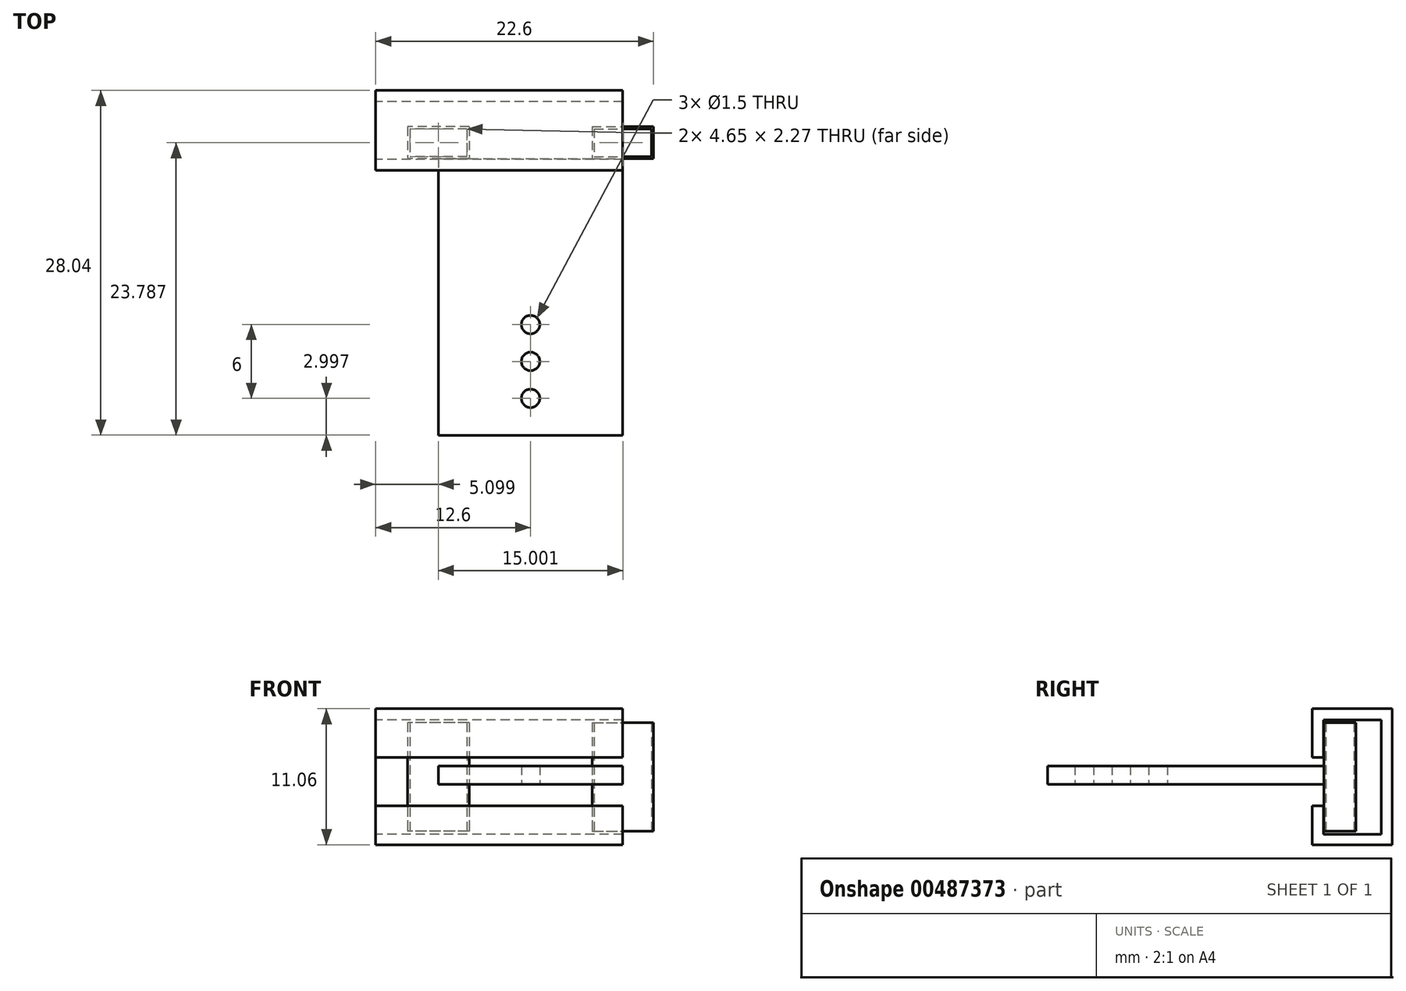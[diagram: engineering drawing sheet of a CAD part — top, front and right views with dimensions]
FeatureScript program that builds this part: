
annotation { "Feature Type Name" : "Feature", "Feature Type Description" : "" }
export const myFeature = defineFeature(function(context is Context, id is Id, definition is map)
    precondition{}
    {
        {
            var Q0;
            Q0=qCreatedBy(makeId("Top.planeOp"),FACE);
            var sketch = newSketch(context, id + "F0", { "sketchPlane" : qUnion([Q0])});
            skLineSegment(sketch, "E0.bottom", {"start": v(-7.5, 5.49) * mm, "end": v(7.5, 5.49) * mm});
            skLineSegment(sketch, "E0.top", {"start": v(-7.5, -17.01) * mm, "end": v(7.5, -17.01) * mm});
            skLineSegment(sketch, "E0.left", {"start": v(-7.5, 5.49) * mm, "end": v(-7.5, -17.01) * mm});
            skLineSegment(sketch, "E0.right", {"start": v(7.5, 5.49) * mm, "end": v(7.5, -17.01) * mm});
            skSolve(sketch);
        }
        {
            var Q0;
            Q0 = qSketchRegion(id + "F0", true);
            extrude(context, id + "F1", {"entities" : qUnion([Q0]), "depth" : 1.5 * mm, "offsetDistance" : 25 * mm});
        }
        {
            var Q0;
            Q0=qCreatedBy(makeId("Top.planeOp"),FACE);
            var sketch = newSketch(context, id + "F2", { "sketchPlane" : qUnion([Q0])});
            skLineSegment(sketch, "E1.bottom", {"start": v(5, 8.07) * mm, "end": v(10, 8.07) * mm});
            skLineSegment(sketch, "E1.top", {"start": v(5, 5.49) * mm, "end": v(10, 5.49) * mm});
            skLineSegment(sketch, "E1.left", {"start": v(5, 8.07) * mm, "end": v(5, 5.49) * mm});
            skLineSegment(sketch, "E1.right", {"start": v(10, 8.07) * mm, "end": v(10, 5.49) * mm});
            skLineSegment(sketch, "E2.MirrorCS", {"start": v(-5, 8.07) * mm, "end": v(-5, 5.49) * mm});
            skLineSegment(sketch, "E3.MirrorCS", {"start": v(-5, 8.07) * mm, "end": v(-10, 8.07) * mm});
            skLineSegment(sketch, "E4.MirrorCS", {"start": v(-10, 8.07) * mm, "end": v(-10, 5.49) * mm});
            skLineSegment(sketch, "E5.MirrorCS", {"start": v(-5, 5.49) * mm, "end": v(-10, 5.49) * mm});
            skLineSegment(sketch, "E6.bottom", {"start": v(5.18, 7.91) * mm, "end": v(9.83, 7.91) * mm});
            skLineSegment(sketch, "E6.top", {"start": v(5.18, 5.64) * mm, "end": v(9.83, 5.64) * mm});
            skLineSegment(sketch, "E6.left", {"start": v(5.18, 7.91) * mm, "end": v(5.18, 5.64) * mm});
            skLineSegment(sketch, "E6.right", {"start": v(9.83, 7.91) * mm, "end": v(9.83, 5.64) * mm});
            skLineSegment(sketch, "E7.MirrorCS", {"start": v(-5.18, 7.91) * mm, "end": v(-9.83, 7.91) * mm});
            skLineSegment(sketch, "E8.MirrorCS", {"start": v(-5.18, 7.91) * mm, "end": v(-5.18, 5.64) * mm});
            skLineSegment(sketch, "E9.MirrorCS", {"start": v(-5.18, 5.64) * mm, "end": v(-9.83, 5.64) * mm});
            skLineSegment(sketch, "E10.MirrorCS", {"start": v(-9.83, 7.91) * mm, "end": v(-9.83, 5.64) * mm});
            skSolve(sketch);
        }
        {
            var Q0;
            Q0 = qSketchRegion(id + "F2", true);
            extrude(context, id + "F3", {"entities" : qUnion([Q0]), "operationType" : NewBodyOperationType.ADD, "depth" : 5 * mm, "offsetDistance" : 25 * mm, "hasSecondDirection" : true, "secondDirectionOppositeDirection" : true, "secondDirectionDepth" : 3.8 * mm});
        }
        {
            var Q0;
            Q0=qCreatedBy(makeId("Top.planeOp"),FACE);
            var sketch = newSketch(context, id + "F4", { "sketchPlane" : qUnion([Q0])});
            skCircle(sketch, "E11", {"center": v(0, -14.01) * mm, "radius": 0.75 * mm});
            skCircle(sketch, "E12", {"center": v(0, -11.01) * mm, "radius": 0.75 * mm});
            skCircle(sketch, "E13", {"center": v(0, -8.01) * mm, "radius": 0.75 * mm});
            skSolve(sketch);
        }
        {
            var Q0;
            Q0 = qSketchRegion(id + "F4", true);
            extrude(context, id + "F5", {"entities" : qUnion([Q0]), "operationType" : NewBodyOperationType.REMOVE, "depth" : 25 * mm, "offsetDistance" : 25 * mm});
        }
        {
            var Q0;
            Q0=qCreatedBy(makeId("Right.planeOp"),FACE);
            var sketch = newSketch(context, id + "F6", { "sketchPlane" : qUnion([Q0])});
            skLineSegment(sketch, "E14", {"start": v(5.43, 2.2) * mm, "end": v(5.43, 5.25) * mm});
            skLineSegment(sketch, "E15", {"start": v(5.43, 5.25) * mm, "end": v(10.13, 5.25) * mm});
            skLineSegment(sketch, "E16", {"start": v(10.13, 5.25) * mm, "end": v(10.13, -4.05) * mm});
            skLineSegment(sketch, "E17", {"start": v(10.13, -4.05) * mm, "end": v(5.43, -4.05) * mm});
            skLineSegment(sketch, "E18", {"start": v(5.43, -4.05) * mm, "end": v(5.43, -1.76) * mm});
            skLineSegment(sketch, "E19", {"start": v(5.43, -1.76) * mm, "end": v(4.53, -1.76) * mm});
            skLineSegment(sketch, "E20", {"start": v(4.53, -1.76) * mm, "end": v(4.53, -4.9) * mm});
            skLineSegment(sketch, "E21", {"start": v(4.53, -4.9) * mm, "end": v(11.03, -4.9) * mm});
            skLineSegment(sketch, "E22", {"start": v(11.03, -4.9) * mm, "end": v(11.03, 6.15) * mm});
            skLineSegment(sketch, "E23", {"start": v(11.03, 6.15) * mm, "end": v(4.53, 6.15) * mm});
            skLineSegment(sketch, "E24", {"start": v(4.53, 6.15) * mm, "end": v(4.53, 2.18) * mm});
            skLineSegment(sketch, "E25", {"start": v(4.53, 2.18) * mm, "end": v(5.43, 2.2) * mm});
            skSolve(sketch);
        }
        {
            var Q0;
            Q0 = qSketchRegion(id + "F6", true);
            extrude(context, id + "F7", {"entities" : qUnion([Q0]), "depth" : 7.5 * mm, "offsetDistance" : 25 * mm, "hasSecondDirection" : true, "secondDirectionOppositeDirection" : true, "secondDirectionDepth" : 12.6 * mm});
        }
    });
